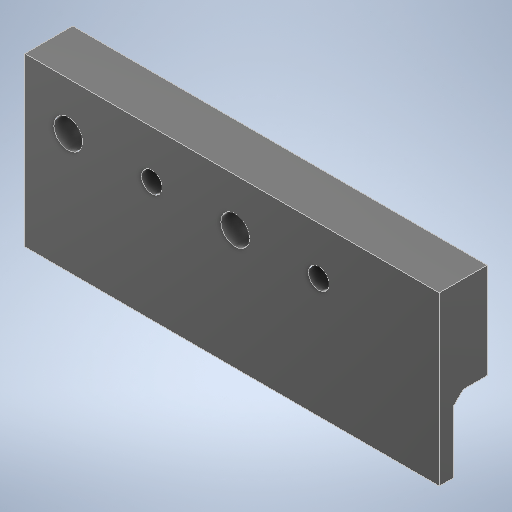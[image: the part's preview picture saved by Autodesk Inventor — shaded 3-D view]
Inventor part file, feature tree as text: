
AUTODESK INVENTOR PART (.ipt)
format: ipt  version: 2025.1 (Build 291241020, 241B)  size: 441,856 bytes
history: native  units: mm
features: sketch x6, extrude x4, hole x2, plane x2, other x2, pattern_linear x1, chamfer x1, reference x1, projected_geometry x1
ambient origin geometry x8: Origin, YZ Plane, XZ Plane, XY Plane, X Axis, Y Axis, Z Axis, Center Point
bodies: Solid1 (feature_tree)
feature tree (20):
  extrude  "Extrusion1"  Depth=20.0mm
  sketch  "Sketch2"  dims[d2=3.0mm d3=0.0mm d5=25.4mm]
  extrude  "Extrusion3"  Depth=3.0mm
  hole  "Hole2"  [1 undecoded]
  hole  "Hole3"  [1 undecoded]
  pattern_linear  "Rectangular Pattern2"  Spacing1=42.6875mm  [1 undecoded]
  chamfer  "Chamfer1"  Distance=34.925mm
  extrude  "Extrusion4"  Depth=5.0mm
  plane  "Work Plane1"
  plane  "Work Plane2"
  extrude  "Extrusion5"  Depth=5.0mm
  sketch  "Sketch1"  dims[d0=260.0mm d1=20.0mm]
  reference  "Reference1"
  sketch  "Sketch5"  dims[d6=12.7mm d31=10.0mm]
  sketch  "Sketch6"  dims[d32=20.0mm d33=10.0mm d34=0.0mm]
  sketch  "Sketch7"  dims[d35=42.6875mm]
  sketch  "Sketch8"  dims[d39=6.0mm d40=6.0mm d41=4.0mm d42=2.0mm d43=90.0deg d44=8.0mm d45=20.594885mm d46=42.6875mm d47=34.925mm d48=34.925mm d49=34.925mm d50=34.925mm d51=10.0mm d52=4.3mm d53=6.0mm d54=4.0mm d55=2.0mm d56=90.0deg d57=6.0mm d58=0.0mm d59=70.0mm d61=34.925mm d62=10.0mm d63=2.0mm d64=2.0mm d65=45.0deg d66=5.0mm d67=0.0mm d68=0.0mm d69=-86.666667mm d70=-173.333333mm d71=0.0mm d72=0.0mm]
  projected_geometry  "Projected Loop1"
  other  "MagDrop4.iam"
  other  "Connect4_RACK:1"
note: 3 required parameter values undecoded (feature->parameter linkage not recoverable at this tier; creation-order binding heuristic only, values carry confidence <= 0.55)
